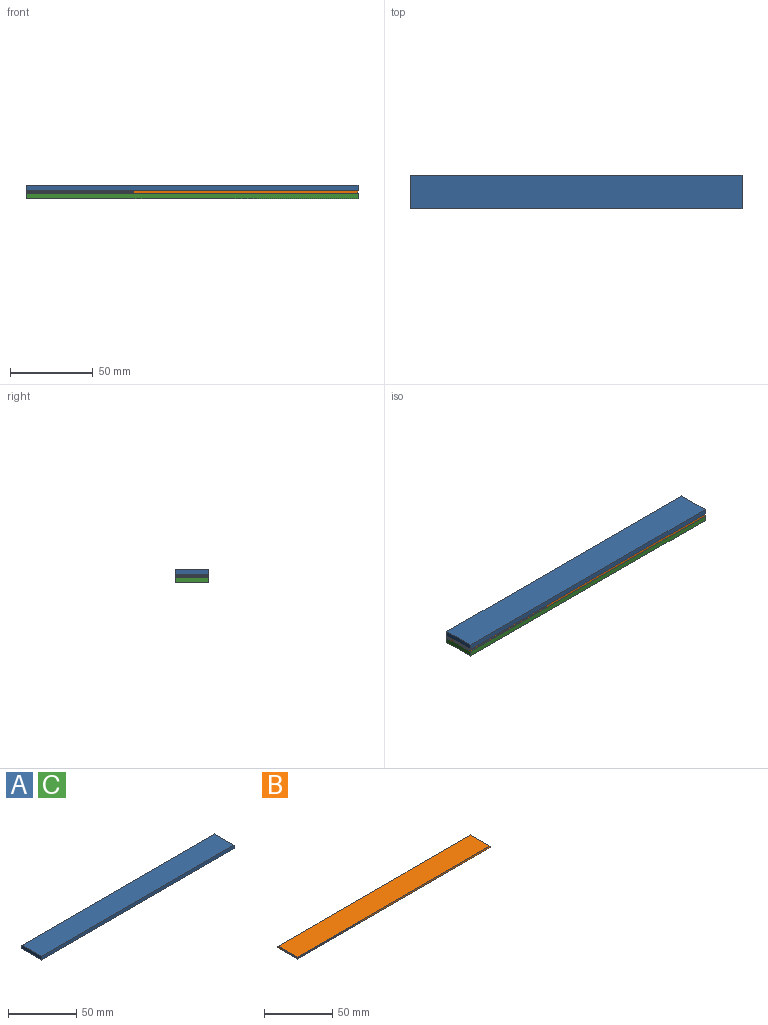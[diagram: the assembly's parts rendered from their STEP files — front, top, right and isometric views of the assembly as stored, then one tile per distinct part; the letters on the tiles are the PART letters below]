
ASSEMBLY  parts=3 mates=1
PART A: 6 faces, bbox 200x20x3.3 mm
  f0: plane 200x20mm, normal (0,0,-1), area 4000mm2, adj f1,f3,f4,f5
  f1: plane 20x3.25mm, normal (1,0,0), area 65mm2, adj f0,f2,f4,f5
  f2: plane 200x20mm, normal (0,0,1), area 4000mm2, adj f1,f3,f4,f5
  f3: plane 20x3.25mm, normal (-1,0,0), area 65mm2, adj f0,f2,f4,f5
  f4: plane 200x3.25mm, normal (0,-1,0), area 650mm2, adj f0,f1,f2,f3
  f5: plane 200x3.25mm, normal (0,1,0), area 650mm2, adj f0,f1,f2,f3
PART B: 10 faces, bbox 200x20x1.6 mm
  f0: plane 20x1.6mm, normal (1,0,0), area 32mm2, adj f1,f7,f8,f9
  f1: plane 200x20mm, normal (0,0,1), area 4000mm2, adj f0,f2,f8,f9
  f2: plane 20x0.79mm, normal (-1,0,0), area 15.8mm2, adj f1,f3,f8,f9
  f3: plane 65x20mm, normal (0,0,-1), area 1300mm2, adj f2,f4,f8,f9
  f4: plane 20x0.02mm, normal (-1,0,0), area 0.4mm2, adj f3,f5,f8,f9
  f5: plane 65x20mm, normal (0,0,1), area 1300mm2, adj f4,f6,f8,f9
  f6: plane 20x0.79mm, normal (-1,0,0), area 15.8mm2, adj f5,f7,f8,f9
  f7: plane 200x20mm, normal (0,0,-1), area 4000mm2, adj f0,f6,f8,f9
  f8: plane 200x1.6mm, normal (0,-1,0), area 318.7mm2, adj f0,f1,f2,f3,f4,f5,f6,f7
  f9: plane 200x1.6mm, normal (0,1,0), area 318.7mm2, adj f0,f1,f2,f3,f4,f5,f6,f7
PART C: same geometry as A
PLACE A t=(-12.05,-16.51,-26.07)mm
PLACE B t=(-12.05,-16.51,-28.5)mm
PLACE C t=(-12.05,-16.51,-30.92)mm
MATE fastened C.f2 <-> B.f7  axis (0,0,1) through (-12.05,-26.51,-29.3)mm
